# Revit family: Double_Sink-American_Standard-Pekoe-18DB6291800.075
name_source: partatom
category: Plumbing Fixtures
revit_build: Autodesk Revit 2018 (Build: 20170223_1515(x64)
units: mm (PartAtom-declared; Revit-internal decimal feet)

## family parameters
Always vertical = No
Cut with Voids When Loaded = Yes
OmniClass Number = 23.45.05.14.14
OmniClass Title = Sinks/Lavatories
Part Type = Normal
Room Calculation Point = No
Round Connector Dimension = Use Diameter
Shared = Yes
Work Plane-Based = Yes

## types (1)
- 18DB6291800.075
    ADA Compliant = Yes
    Assembly Code = D2010410
    Basin Shape = Rectangular
    Bowl Length = 16"
    Bowl Width = 13"
    CW Connection = Yes
    CWFU = 2
    Cold Water Connection Diameter = 1/2"
    Cold Water Connection Radius = 1/4"
    Cold Water Connection Width = 4"
    Default Elevation = 34"
    Description = Pekoe 29x18-inch ADA Double Bowl Stainless Steel Kitchen Sink. The Pekoe ADA Double Bowl Stainless Steel Sink from American Standard takes your kitchen to the next level of sophisticated style and functionality. The double bowl design offers convenience and versatility during prep and clean-up. This ADA compliant sink is 6” deep for easy accessibility and features bottom and side sound pads for reduced noise and vibration. Multilayer spray insulation ensures optimal protection against scratches, heat, and condensation. Made of durable 18-gauge stainless steel, it pairs perfectly with Pekoe Kitchen Faucets.  Includes drains and coordinating grids for added protection.
    Finish = Metal-American_Standard-075-Stainless_Steel
    Gap = 1"
    HW Connection = Yes
    HWFU = 2
    Height = 6"
    Hot Water Connection Diameter = 1"
    Hot Water Connection Radius = 1/4"
    Hot Water Connection Width = 4"
    IAPMO Compliance = ASME A112.19.3
    Installation Type = Undermount
    Length = 18"
    Manufacturer = American Standard
    Material = Metal-American_Standard-075-Stainless_Steel
    Model = 18DB6291800.075
    Price = Prices may vary. Please consult Manufacturer Representative for most up-to-date price list.
    Product Documentation Link = https://www.americanstandard-us.com
    Product Page URL = https://www.americanstandard-us.com
    Revised Date = 03/31/2021
    Type Comments = 32" (813mm) cabinet required
    URL = https://www.americanstandard-us.com
    Vent Connection = No
    WFU = 3
    Warranty Documentation Link = https://www.americanstandard-us.com
    Waste Connection = Yes
    Waste Connection Diameter = 1 1/2"
    Waste Connection Offset = 6 5/16"
    Waste Connection Radius = 3/4"
    Waste Connection Width = 7 1/2"
    Width = 29"

## geometry (parser evidence)
native form markers: Sweep x2
no freeform markers — native parametric forms only
